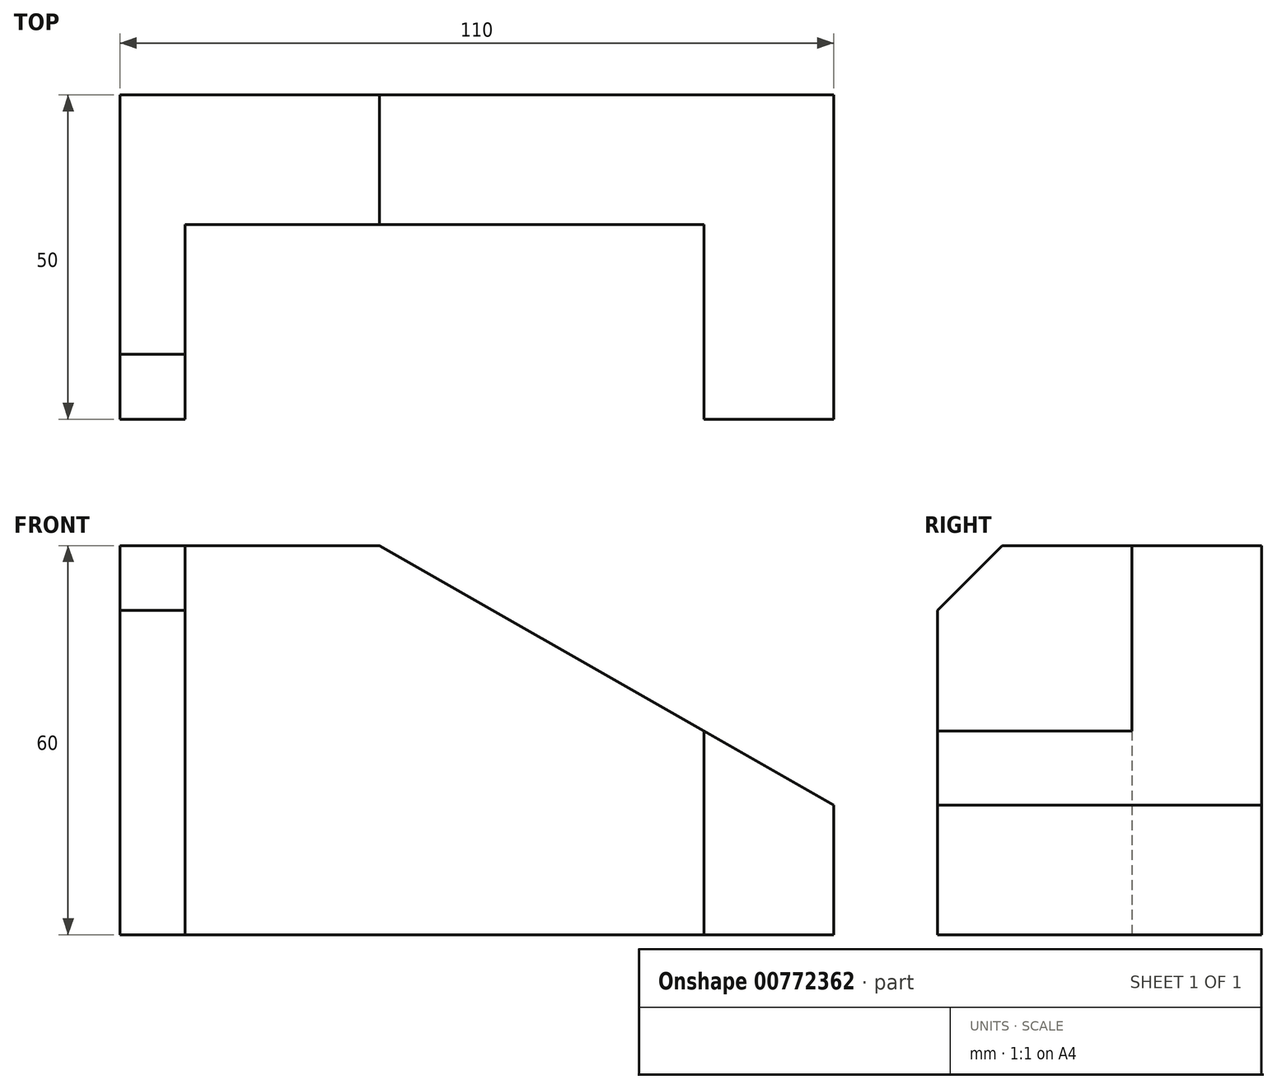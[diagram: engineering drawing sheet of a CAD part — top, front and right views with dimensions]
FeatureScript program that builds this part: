
annotation { "Feature Type Name" : "Feature", "Feature Type Description" : "" }
export const myFeature = defineFeature(function(context is Context, id is Id, definition is map)
    precondition{}
    {
        {
            var Q0;
            Q0=qCreatedBy(makeId("Top.planeOp"),FACE);
            var sketch = newSketch(context, id + "F0", { "sketchPlane" : qUnion([Q0])});
            skLineSegment(sketch, "E0.bottom", {"start": v(55, 25) * mm, "end": v(-55, 25) * mm});
            skLineSegment(sketch, "E0.top", {"start": v(55, -25) * mm, "end": v(35, -25) * mm});
            skLineSegment(sketch, "E0.left", {"start": v(55, 25) * mm, "end": v(55, -25) * mm});
            skLineSegment(sketch, "E0.right", {"start": v(-55, 25) * mm, "end": v(-55, -25) * mm});
            skPoint(sketch, "E0.middle", {"position": v(0, 0) * mm});
            skLineSegment(sketch, "E1", {"start": v(-45, -25) * mm, "end": v(-45, 5) * mm});
            skLineSegment(sketch, "E2", {"start": v(-45, 5) * mm, "end": v(35, 5) * mm});
            skLineSegment(sketch, "E3", {"start": v(35, 5) * mm, "end": v(35, -25) * mm});
            skLineSegment(sketch, "E4.trimOffspring", {"start": v(-45, -25) * mm, "end": v(-55, -25) * mm});
            skSolve(sketch);
        }
        {
            var Q0;
            Q0 = qSketchRegion(id + "F0", true);
            extrude(context, id + "F1", {"entities" : qUnion([Q0]), "depth" : 60 * mm, "offsetDistance" : 25 * mm});
        }
        {
            var Q0;
            Q0=makeQuery(id+"F1.opExtrude","CAP_EDGE",EDGE,{"disambiguationData":[OSD([sQuery(id+"F0.wireOp",EDGE,"E0.left")])],"isStart":false});
            chamfer(context, id + "F2", {"entities" : qUnion([Q0]), "chamferType" : ChamferType.TWO_OFFSETS, "width1" : 40 * mm, "oppositeDirection" : false, "width2" : 70 * mm, "tangentPropagation" : true});
        }
        {
            var Q0;
            Q0=makeQuery(id+"F1.opExtrude","CAP_EDGE",EDGE,{"disambiguationData":[OSD([sQuery(id+"F0.wireOp",EDGE,"E4.trimOffspring")])],"isStart":false});
            chamfer(context, id + "F3", {"entities" : qUnion([Q0]), "width" : 10 * mm, "tangentPropagation" : true});
        }
    });
